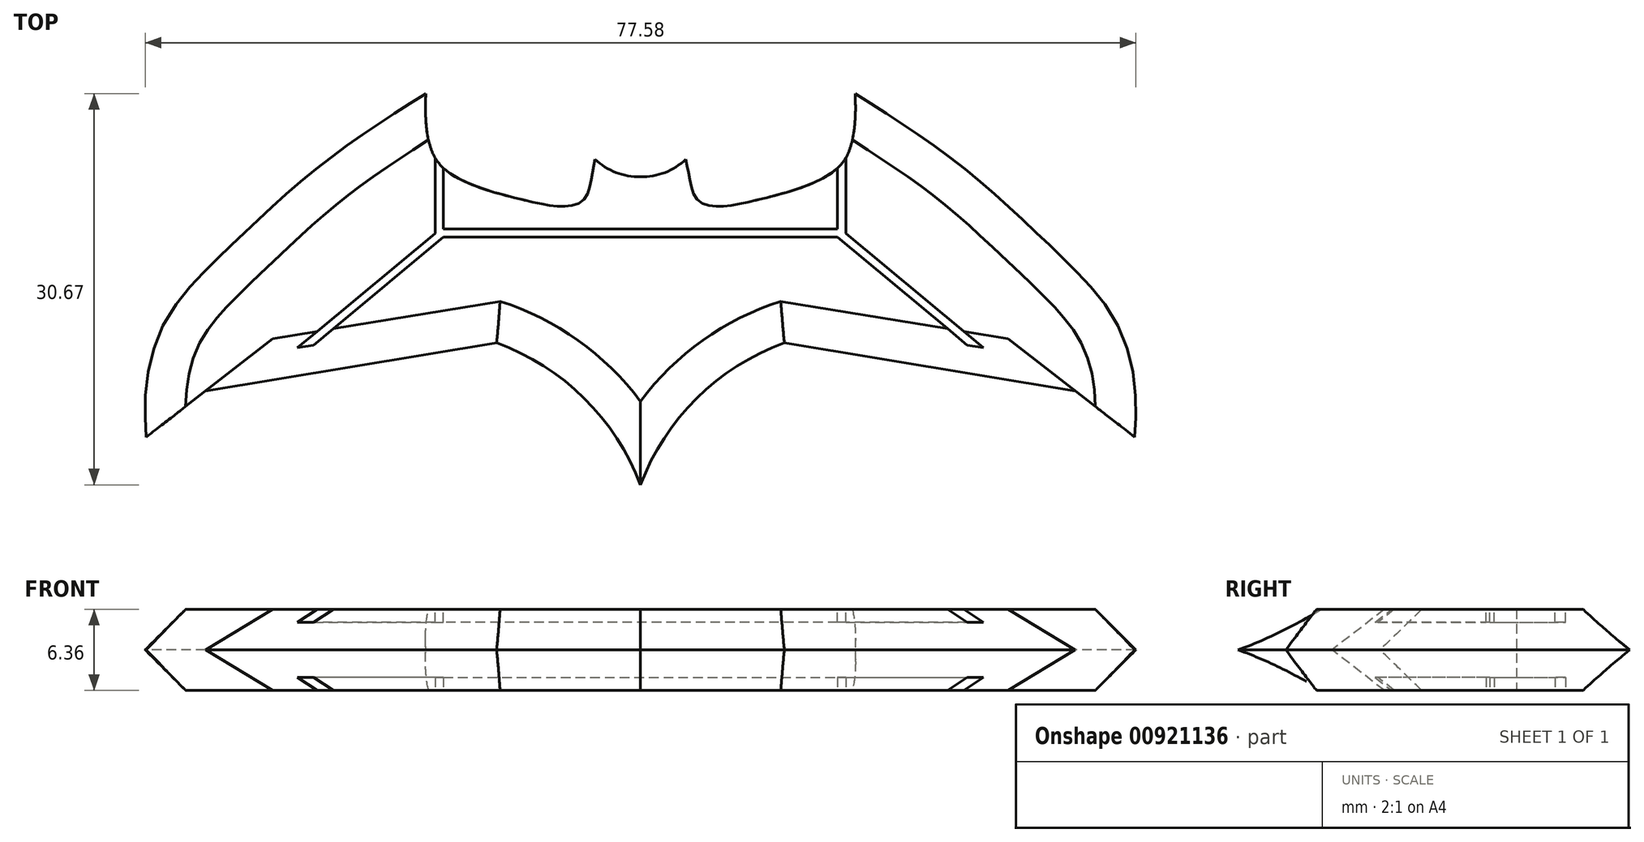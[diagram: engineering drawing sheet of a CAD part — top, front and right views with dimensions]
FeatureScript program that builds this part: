
annotation { "Feature Type Name" : "Feature", "Feature Type Description" : "" }
export const myFeature = defineFeature(function(context is Context, id is Id, definition is map)
    precondition{}
    {
        {
            var Q0;
            Q0=qCreatedBy(makeId("Top.planeOp"),FACE);
            var sketch = newSketch(context, id + "F0", { "sketchPlane" : qUnion([Q0])});
            skArc(sketch, "E0", {"start": v(16.8, -26.82) * mm, "mid": v(12.4, -20.02) * mm, "end": v(5.55, -15.7) * mm});
            skLineSegment(sketch, "E1", {"start": v(5.55, -15.7) * mm, "end": v(-17.23, -19.45) * mm});
            skLineSegment(sketch, "E2", {"start": v(-17.23, -19.45) * mm, "end": v(-21.9, -23.07) * mm});
            skFitSpline(sketch, "E3", {"points": [v(-21.9, -23.07) * mm, v(-21.9, -18.93) * mm, v(-20.34, -13.88) * mm, v(-16.97, -9.74) * mm, v(-13.6, -6.5) * mm, v(-8.17, -1.71) * mm, v(0, 3.85) * mm], "startDerivative": vector(-1.73, 28.9) * mm, "endDerivative": vector(39.9, 25.47) * mm});
            skFitSpline(sketch, "E4", {"points": [v(0, 3.85) * mm, v(0, 1.82) * mm, v(0.69, -1.11) * mm, v(2.68, -2.87) * mm, v(5.74, -3.99) * mm, v(8.85, -4.75) * mm, v(10.9, -4.98) * mm, v(12.37, -4.46) * mm, v(12.95, -2.87) * mm, v(13.25, -1.29) * mm], "startDerivative": vector(-0.66, -18.08) * mm, "endDerivative": vector(3.02, 16.48) * mm});
            skArc(sketch, "E5", {"start": v(13.25, -1.29) * mm, "mid": v(14.9, -2.33) * mm, "end": v(16.8, -2.67) * mm});
            skArc(sketch, "E6.MirrorCS", {"start": v(20.37, -1.29) * mm, "mid": v(18.73, -2.33) * mm, "end": v(16.8, -2.67) * mm});
            skArc(sketch, "E7.MirrorCS", {"start": v(16.8, -26.82) * mm, "mid": v(21.22, -20.02) * mm, "end": v(28.07, -15.7) * mm});
            skLineSegment(sketch, "E8.MirrorCS", {"start": v(28.07, -15.7) * mm, "end": v(50.85, -19.45) * mm});
            skLineSegment(sketch, "E9.MirrorCS", {"start": v(50.85, -19.45) * mm, "end": v(55.51, -23.07) * mm});
            skFitSpline(sketch, "E10.MirrorCS", {"points": [v(55.51, -23.07) * mm, v(55.51, -18.93) * mm, v(53.96, -13.88) * mm, v(50.6, -9.74) * mm, v(47.23, -6.5) * mm, v(41.8, -1.71) * mm, v(33.62, 3.85) * mm], "startDerivative": vector(1.73, 28.9) * mm, "endDerivative": vector(-39.9, 25.47) * mm});
            skFitSpline(sketch, "E11.MirrorCS", {"points": [v(33.62, 3.85) * mm, v(33.62, 1.82) * mm, v(32.93, -1.11) * mm, v(30.94, -2.87) * mm, v(27.88, -3.99) * mm, v(24.77, -4.75) * mm, v(22.72, -4.98) * mm, v(21.25, -4.46) * mm, v(20.66, -2.87) * mm, v(20.37, -1.29) * mm], "startDerivative": vector(0.66, -18.08) * mm, "endDerivative": vector(-3.02, 16.48) * mm});
            skSolve(sketch);
        }
        {
            var Q0;
            Q0=makeQuery(id+"F0.imprint","IMPRINT",FACE,{"disambiguationData":[TD([[makeQuery(id+"F0.imprint","IMPRINT",EDGE,{"derivedFrom":sQuery(id+"F0.wireOp",EDGE,"E0")}),-1.0]])]});
            extrude(context, id + "F1", {"entities" : qUnion([Q0]), "offsetDistance" : 25.4 * mm, "depth" : 3.17 * mm});
        }
        {
            var Q0;
            Q0=makeQuery(id+"F1.opExtrude","CAP_FACE",FACE,{"disambiguationData":[OSD([sQuery(id+"F0.wireOp",EDGE,"E0"),sQuery(id+"F0.wireOp",EDGE,"E1"),sQuery(id+"F0.wireOp",EDGE,"E2"),sQuery(id+"F0.wireOp",EDGE,"E3"),sQuery(id+"F0.wireOp",EDGE,"E4"),sQuery(id+"F0.wireOp",EDGE,"E5"),sQuery(id+"F0.wireOp",EDGE,"E6.MirrorCS"),sQuery(id+"F0.wireOp",EDGE,"E7.MirrorCS"),sQuery(id+"F0.wireOp",EDGE,"E8.MirrorCS"),sQuery(id+"F0.wireOp",EDGE,"E9.MirrorCS"),sQuery(id+"F0.wireOp",EDGE,"E10.MirrorCS"),sQuery(id+"F0.wireOp",EDGE,"E11.MirrorCS")])],"isStart":false});
            var sketch = newSketch(context, id + "F2", { "sketchPlane" : qUnion([Q0])});
            skLineSegment(sketch, "E12", {"start": v(-12.05, -18.6) * mm, "end": v(1.38, -7.4) * mm});
            skLineSegment(sketch, "E13", {"start": v(1.38, -6.75) * mm, "end": v(1.38, -1.99) * mm});
            skLineSegment(sketch, "E14", {"start": v(16.8, -2.67) * mm, "end": v(16.8, -26.82) * mm});
            skLineSegment(sketch, "E15", {"start": v(1.38, -7.4) * mm, "end": v(16.8, -7.4) * mm});
            skLineSegment(sketch, "E16", {"start": v(1.38, -6.75) * mm, "end": v(16.8, -6.75) * mm});
            skLineSegment(sketch, "E17.MirrorCS", {"start": v(32.24, -6.75) * mm, "end": v(16.8, -6.75) * mm});
            skLineSegment(sketch, "E18.MirrorCS", {"start": v(32.24, -7.4) * mm, "end": v(16.8, -7.4) * mm});
            skLineSegment(sketch, "E19.MirrorCS", {"start": v(32.24, -6.75) * mm, "end": v(32.24, -1.99) * mm});
            skLineSegment(sketch, "E20.MirrorCS", {"start": v(45.67, -18.6) * mm, "end": v(32.24, -7.4) * mm});
            skLineSegment(sketch, "E21", {"start": v(0.73, -6.75) * mm, "end": v(0.73, -1.18) * mm});
            skLineSegment(sketch, "E22", {"start": v(32.9, -6.75) * mm, "end": v(32.9, -1.18) * mm});
            skLineSegment(sketch, "E23", {"start": v(0.73, -7.1) * mm, "end": v(-13.07, -18.6) * mm});
            skLineSegment(sketch, "E24", {"start": v(0.73, -6.75) * mm, "end": v(0.73, -7.1) * mm});
            skLineSegment(sketch, "E25", {"start": v(46.1, -18.1) * mm, "end": v(32.9, -7.1) * mm});
            skLineSegment(sketch, "E26", {"start": v(32.9, -6.75) * mm, "end": v(32.9, -7.1) * mm});
            skLineSegment(sketch, "E27", {"start": v(32.9, -7.1) * mm, "end": v(46.94, -18.8) * mm});
            skLineSegment(sketch, "E28", {"start": v(45.67, -18.6) * mm, "end": v(46.94, -18.8) * mm});
            skLineSegment(sketch, "E29", {"start": v(-13.07, -18.6) * mm, "end": v(-13.32, -18.8) * mm});
            skLineSegment(sketch, "E30", {"start": v(-13.32, -18.8) * mm, "end": v(-12.05, -18.6) * mm});
            skLineSegment(sketch, "E31", {"start": v(-12.05, -18.6) * mm, "end": v(-13.32, -18.8) * mm});
            skSolve(sketch);
        }
        {
            var Q0;
            {var subQ4=sQuery(id+"F2.wireOp",EDGE,"cyNa1HoE-043t-gLWv-W5ku-b2fROLpZmleC");Q0=makeQuery(id+"F2.imprint","IMPRINT",FACE,{"disambiguationData":[TD([[makeQuery(id+"F2.imprint","IMPRINT",EDGE,{"derivedFrom":subQ4}),1.0]])]});}
            var Q1;
            {var subQ3=sQuery(id+"F2.wireOp",EDGE,"E17.MirrorCS");Q1=makeQuery(id+"F2.imprint","IMPRINT",FACE,{"disambiguationData":[TD([[makeQuery(id+"F2.imprint","IMPRINT",EDGE,{"derivedFrom":subQ3}),1.0]])]});}
            var Q2;
            Q2=makeQuery(id+"F2.imprint","IMPRINT",FACE,{"disambiguationData":[TD([[makeQuery(id+"F2.imprint","IMPRINT",EDGE,{"derivedFrom":sQuery(id+"F2.wireOp",EDGE,"E12")}),1.0]])]});
            extrude(context, id + "F3", {"entities" : qUnion([Q0, Q1, Q2]), "operationType" : NewBodyOperationType.REMOVE, "oppositeDirection" : true, "offsetDistance" : 25.4 * mm, "depth" : 1.02 * mm});
        }
        {
            var Q0;
            Q0=makeQuery(id+"F1.opExtrude","CAP_EDGE",EDGE,{"disambiguationData":[OSD([sQuery(id+"F0.wireOp",EDGE,"E3")])],"isStart":false});
            var Q1;
            Q1=makeQuery(id+"F1.opExtrude","CAP_EDGE",EDGE,{"disambiguationData":[OSD([sQuery(id+"F0.wireOp",EDGE,"E10.MirrorCS")])],"isStart":false});
            chamfer(context, id + "F4", {"entities" : qUnion([Q0, Q1]), "width" : 3.17 * mm, "tangentPropagation" : true});
        }
        {
            var Q0;
            Q0=makeQuery(id+"F1.opExtrude","CAP_FACE",FACE,{"disambiguationData":[OSD([sQuery(id+"F0.wireOp",EDGE,"E0"),sQuery(id+"F0.wireOp",EDGE,"E1"),sQuery(id+"F0.wireOp",EDGE,"E2"),sQuery(id+"F0.wireOp",EDGE,"E3"),sQuery(id+"F0.wireOp",EDGE,"E4"),sQuery(id+"F0.wireOp",EDGE,"E5"),sQuery(id+"F0.wireOp",EDGE,"E6.MirrorCS"),sQuery(id+"F0.wireOp",EDGE,"E7.MirrorCS"),sQuery(id+"F0.wireOp",EDGE,"E8.MirrorCS"),sQuery(id+"F0.wireOp",EDGE,"E9.MirrorCS"),sQuery(id+"F0.wireOp",EDGE,"E10.MirrorCS"),sQuery(id+"F0.wireOp",EDGE,"E11.MirrorCS")])],"isStart":true});
            extrude(context, id + "F5", {"entities" : qUnion([Q0]), "operationType" : NewBodyOperationType.ADD, "depth" : 3.17 * mm, "offsetDistance" : 25.4 * mm});
        }
        {
            var Q0;
            {var subQ0=sQuery(id+"F0.wireOp",EDGE,"E11.MirrorCS");var subQ1=sQuery(id+"F0.wireOp",EDGE,"E10.MirrorCS");var subQ2=sQuery(id+"F0.wireOp",EDGE,"E9.MirrorCS");var subQ3=sQuery(id+"F0.wireOp",EDGE,"E8.MirrorCS");var subQ4=sQuery(id+"F0.wireOp",EDGE,"E7.MirrorCS");var subQ5=sQuery(id+"F0.wireOp",EDGE,"E6.MirrorCS");var subQ6=sQuery(id+"F0.wireOp",EDGE,"E5");var subQ7=sQuery(id+"F0.wireOp",EDGE,"E4");var subQ8=sQuery(id+"F0.wireOp",EDGE,"E3");var subQ9=sQuery(id+"F0.wireOp",EDGE,"E2");var subQ10=sQuery(id+"F0.wireOp",EDGE,"E1");var subQ11=sQuery(id+"F0.wireOp",EDGE,"E0");Q0=makeQuery(id+"F5.opExtrude","CAP_EDGE",EDGE,{"disambiguationData":[OSD([subQ11,subQ10,subQ9,subQ8,subQ7,subQ6,subQ5,subQ4,subQ3,subQ2,subQ1,subQ0]),TDD([makeQuery(id+"F4.opChamfer","BLEND_EDGE",EDGE,{"blendedFrom":[makeQuery(id+"F1.opExtrude","CAP_EDGE",EDGE,{"disambiguationData":[OSD([subQ1])],"isStart":false}),makeQuery(id+"F1.opExtrude","CAP_FACE",FACE,{"disambiguationData":[OSD([subQ11,subQ10,subQ9,subQ8,subQ7,subQ6,subQ5,subQ4,subQ3,subQ2,subQ1,subQ0])],"isStart":true})],"blendedInto":[makeQuery(id+"F1.opExtrude","CAP_FACE",FACE,{"disambiguationData":[OSD([subQ11,subQ10,subQ9,subQ8,subQ7,subQ6,subQ5,subQ4,subQ3,subQ2,subQ1,subQ0])],"isStart":true})]})])],"isStart":false});}
            chamfer(context, id + "F6", {"entities" : qUnion([Q0]), "width" : 3.17 * mm, "tangentPropagation" : true});
        }
        {
            var Q0;
            Q0=makeQuery(id+"F5.opExtrude","CAP_EDGE",EDGE,{"disambiguationData":[OSD([sQuery(id+"F0.wireOp",EDGE,"E10.MirrorCS")])],"isStart":false});
            var Q1;
            Q1=makeQuery(id+"F5.opExtrude","CAP_EDGE",EDGE,{"disambiguationData":[OSD([sQuery(id+"F0.wireOp",EDGE,"E3")])],"isStart":false});
            chamfer(context, id + "F7", {"entities" : qUnion([Q0, Q1]), "width" : 3.18 * mm, "tangentPropagation" : true});
        }
        {
            var Q0;
            Q0=makeQuery(id+"F5.opExtrude","CAP_FACE",FACE,{"disambiguationData":[OSD([sQuery(id+"F0.wireOp",EDGE,"E0"),sQuery(id+"F0.wireOp",EDGE,"E1"),sQuery(id+"F0.wireOp",EDGE,"E2"),sQuery(id+"F0.wireOp",EDGE,"E3"),sQuery(id+"F0.wireOp",EDGE,"E4"),sQuery(id+"F0.wireOp",EDGE,"E5"),sQuery(id+"F0.wireOp",EDGE,"E6.MirrorCS"),sQuery(id+"F0.wireOp",EDGE,"E7.MirrorCS"),sQuery(id+"F0.wireOp",EDGE,"E8.MirrorCS"),sQuery(id+"F0.wireOp",EDGE,"E9.MirrorCS"),sQuery(id+"F0.wireOp",EDGE,"E10.MirrorCS"),sQuery(id+"F0.wireOp",EDGE,"E11.MirrorCS")])],"isStart":false});
            var sketch = newSketch(context, id + "F8", { "sketchPlane" : qUnion([Q0])});
            skLineSegment(sketch, "E32", {"start": v(16.8, 2.67) * mm, "end": v(16.8, 26.82) * mm});
            skLineSegment(sketch, "E33", {"start": v(16.8, 26.82) * mm, "end": v(16.8, 7.4) * mm});
            skLineSegment(sketch, "E34", {"start": v(16.8, 7.4) * mm, "end": v(1.38, 7.4) * mm});
            skLineSegment(sketch, "E35", {"start": v(1.38, 6.75) * mm, "end": v(16.8, 6.75) * mm});
            skLineSegment(sketch, "E36", {"start": v(16.8, 7.4) * mm, "end": v(32.24, 7.4) * mm});
            skLineSegment(sketch, "E37", {"start": v(16.8, 6.75) * mm, "end": v(32.24, 6.75) * mm});
            skLineSegment(sketch, "E38", {"start": v(1.38, 7.4) * mm, "end": v(-12.05, 18.6) * mm});
            skLineSegment(sketch, "E39", {"start": v(32.24, 7.4) * mm, "end": v(45.67, 18.6) * mm});
            skLineSegment(sketch, "E40", {"start": v(0.73, 7.1) * mm, "end": v(0.73, 1.18) * mm});
            skPoint(sketch, "E41.orphan", {"position": v(0.73, 7.4) * mm});
            skLineSegment(sketch, "E42", {"start": v(0.73, 7.1) * mm, "end": v(-12.47, 18.1) * mm});
            skLineSegment(sketch, "E43", {"start": v(32.24, 6.75) * mm, "end": v(32.24, 1.99) * mm});
            skPoint(sketch, "E44.endSnap0", {"position": v(32.7, 6.65) * mm});
            skLineSegment(sketch, "E45", {"start": v(32.9, 1.18) * mm, "end": v(32.24, 1.99) * mm});
            skLineSegment(sketch, "E46", {"start": v(32.9, 1.18) * mm, "end": v(32.9, 7.1) * mm});
            skLineSegment(sketch, "E47", {"start": v(32.9, 7.1) * mm, "end": v(46.1, 18.1) * mm});
            skLineSegment(sketch, "E48", {"start": v(46.1, 18.1) * mm, "end": v(46.94, 18.8) * mm});
            skLineSegment(sketch, "E49", {"start": v(46.94, 18.8) * mm, "end": v(45.67, 18.6) * mm});
            skLineSegment(sketch, "E50", {"start": v(0.73, 7.1) * mm, "end": v(-13.32, 18.8) * mm});
            skLineSegment(sketch, "E51", {"start": v(-13.32, 18.8) * mm, "end": v(-12.05, 18.6) * mm});
            skLineSegment(sketch, "E52", {"start": v(1.38, 6.75) * mm, "end": v(1.38, 1.99) * mm});
            skLineSegment(sketch, "E53", {"start": v(45.67, 18.6) * mm, "end": v(46.94, 18.8) * mm});
            skLineSegment(sketch, "E54", {"start": v(46.94, 18.8) * mm, "end": v(32.9, 7.1) * mm});
            skLineSegment(sketch, "E55", {"start": v(32.9, 1.18) * mm, "end": v(32.9, 0.48) * mm});
            skLineSegment(sketch, "E56", {"start": v(32.9, 0.48) * mm, "end": v(32.24, 0.48) * mm});
            skLineSegment(sketch, "E57", {"start": v(32.24, 0.48) * mm, "end": v(32.24, 1.99) * mm});
            skSolve(sketch);
        }
        {
            var Q0;
            Q0 = qSketchRegion(id + "F8", true);
            var Q1;
            {var subQ4=sQuery(id+"F8.wireOp",EDGE,"E34");Q1=makeQuery(id+"F8.imprint","IMPRINT",FACE,{"disambiguationData":[TD([[makeQuery(id+"F8.imprint","IMPRINT",EDGE,{"derivedFrom":subQ4}),1.0]])]});}
            extrude(context, id + "F9", {"entities" : qUnion([Q0, Q1]), "operationType" : NewBodyOperationType.REMOVE, "oppositeDirection" : true, "depth" : 1.02 * mm, "offsetDistance" : 25.4 * mm});
        }
        {
            var Q0;
            {var subQ0=sQuery(id+"F0.wireOp",EDGE,"E8.MirrorCS");var subQ1=sQuery(id+"F0.wireOp",EDGE,"E7.MirrorCS");Q0=makeQuery(id+"F9.boolean.opBoolean","SPLIT",EDGE,{"disambiguationData":[TD([makeQuery(id+"F1.opExtrude","SWEPT_FACE",FACE,{"disambiguationData":[OSD([subQ1])]})])],"derivedFrom":makeQuery(id+"F5.opExtrude","CAP_EDGE",EDGE,{"disambiguationData":[OSD([subQ0])],"isStart":false})});}
            var Q1;
            Q1=makeQuery(id+"F5.opExtrude","CAP_EDGE",EDGE,{"disambiguationData":[OSD([sQuery(id+"F0.wireOp",EDGE,"E7.MirrorCS")])],"isStart":false});
            var Q2;
            Q2=makeQuery(id+"F5.opExtrude","CAP_EDGE",EDGE,{"disambiguationData":[OSD([sQuery(id+"F0.wireOp",EDGE,"E0")])],"isStart":false});
            var Q3;
            {var subQ0=sQuery(id+"F0.wireOp",EDGE,"E1");var subQ1=sQuery(id+"F0.wireOp",EDGE,"E0");Q3=makeQuery(id+"F9.boolean.opBoolean","SPLIT",EDGE,{"disambiguationData":[TD([makeQuery(id+"F1.opExtrude","SWEPT_FACE",FACE,{"disambiguationData":[OSD([subQ1])]})])],"derivedFrom":makeQuery(id+"F5.opExtrude","CAP_EDGE",EDGE,{"disambiguationData":[OSD([subQ0])],"isStart":false})});}
            chamfer(context, id + "F10", {"entities" : qUnion([Q0, Q1, Q2, Q3]), "width" : 3.18 * mm, "tangentPropagation" : true});
        }
        {
            var Q0;
            {var subQ0=sQuery(id+"F0.wireOp",EDGE,"E0");var subQ1=sQuery(id+"F0.wireOp",EDGE,"E1");Q0=makeQuery(id+"F3.boolean.opBoolean","SPLIT",EDGE,{"disambiguationData":[TD([makeQuery(id+"F1.opExtrude","SWEPT_FACE",FACE,{"disambiguationData":[OSD([subQ0])]})])],"derivedFrom":makeQuery(id+"F1.opExtrude","CAP_EDGE",EDGE,{"disambiguationData":[OSD([subQ1])],"isStart":false})});}
            var Q1;
            Q1=makeQuery(id+"F1.opExtrude","CAP_EDGE",EDGE,{"disambiguationData":[OSD([sQuery(id+"F0.wireOp",EDGE,"E0")])],"isStart":false});
            var Q2;
            Q2=makeQuery(id+"F1.opExtrude","CAP_EDGE",EDGE,{"disambiguationData":[OSD([sQuery(id+"F0.wireOp",EDGE,"E7.MirrorCS")])],"isStart":false});
            var Q3;
            {var subQ0=sQuery(id+"F0.wireOp",EDGE,"E8.MirrorCS");var subQ1=sQuery(id+"F0.wireOp",EDGE,"E7.MirrorCS");Q3=makeQuery(id+"F3.boolean.opBoolean","SPLIT",EDGE,{"disambiguationData":[TD([makeQuery(id+"F1.opExtrude","SWEPT_FACE",FACE,{"disambiguationData":[OSD([subQ1])]})])],"derivedFrom":makeQuery(id+"F1.opExtrude","CAP_EDGE",EDGE,{"disambiguationData":[OSD([subQ0])],"isStart":false})});}
            chamfer(context, id + "F11", {"entities" : qUnion([Q0, Q1, Q2, Q3]), "width" : 3.18 * mm, "tangentPropagation" : true});
        }
    });
